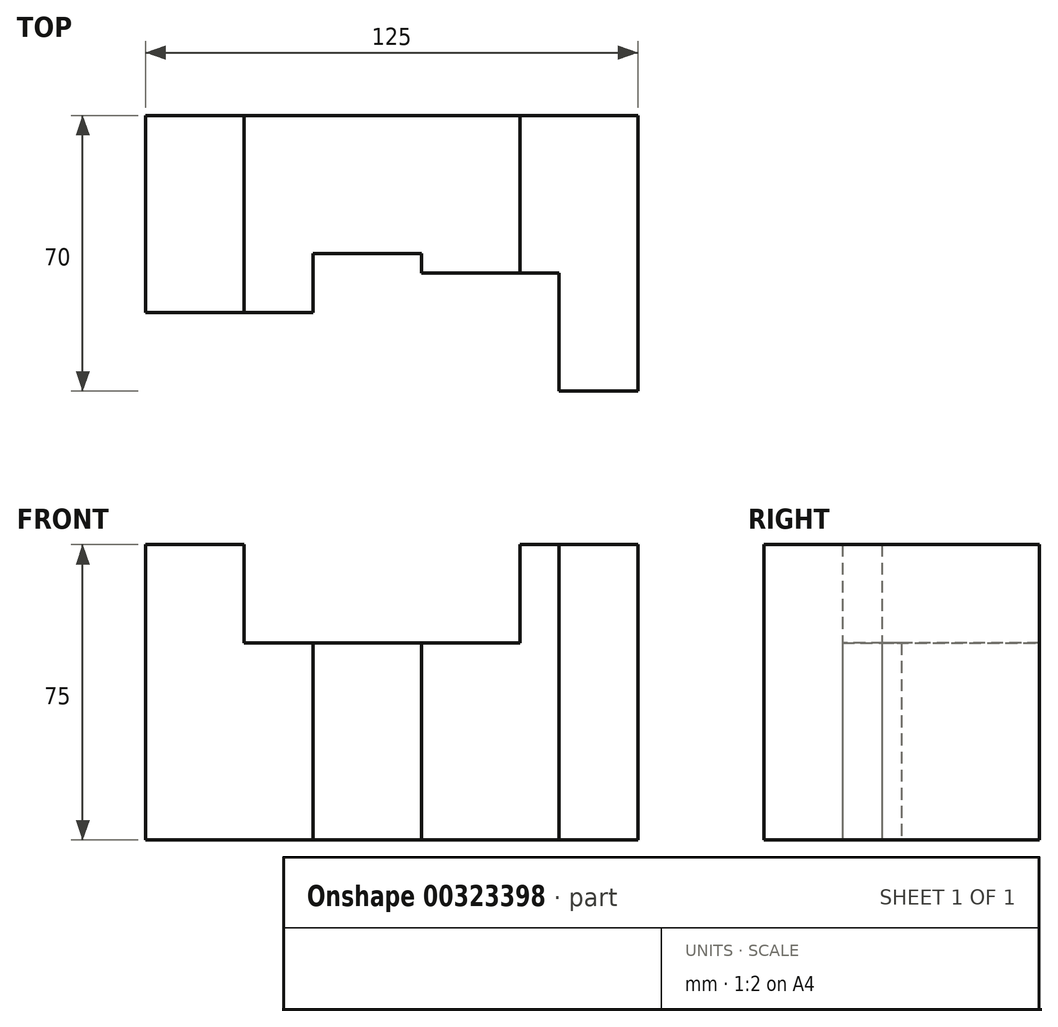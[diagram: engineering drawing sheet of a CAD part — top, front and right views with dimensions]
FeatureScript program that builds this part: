
annotation { "Feature Type Name" : "Feature", "Feature Type Description" : "" }
export const myFeature = defineFeature(function(context is Context, id is Id, definition is map)
    precondition{}
    {
        {
            var Q0;
            Q0=qCreatedBy(makeId("Top.planeOp"),FACE);
            var sketch = newSketch(context, id + "F0", { "sketchPlane" : qUnion([Q0])});
            skLineSegment(sketch, "E0.bottom", {"start": v(0, 0) * mm, "end": v(25, 0) * mm});
            skLineSegment(sketch, "E0.top", {"start": v(0, 50) * mm, "end": v(25, 50) * mm});
            skLineSegment(sketch, "E0.left", {"start": v(0, 0) * mm, "end": v(0, 50) * mm});
            skLineSegment(sketch, "E0.right", {"start": v(25, 0) * mm, "end": v(25, 50) * mm});
            skSolve(sketch);
        }
        {
            var Q0;
            Q0 = qSketchRegion(id + "F0", true);
            extrude(context, id + "F1", {"entities" : qUnion([Q0]), "depth" : (15 * 5) * mm});
        }
        {
            var Q0;
            Q0=qCreatedBy(makeId("Top.planeOp"),FACE);
            var sketch = newSketch(context, id + "F2", { "sketchPlane" : qUnion([Q0])});
            skLineSegment(sketch, "E1", {"start": v(25, 0) * mm, "end": v(25, 50) * mm});
            skLineSegment(sketch, "E2", {"start": v(25, 50) * mm, "end": v(95, 50) * mm});
            skLineSegment(sketch, "E3", {"start": v(95, 50) * mm, "end": v(95, 10) * mm});
            skLineSegment(sketch, "E4", {"start": v(95, 10) * mm, "end": v(70, 10) * mm});
            skLineSegment(sketch, "E5", {"start": v(70, 10) * mm, "end": v(70, 15) * mm});
            skLineSegment(sketch, "E6", {"start": v(70, 15) * mm, "end": v(42.5, 15) * mm});
            skLineSegment(sketch, "E7", {"start": v(42.5, 15) * mm, "end": v(42.5, 0) * mm});
            skLineSegment(sketch, "E8", {"start": v(42.5, 0) * mm, "end": v(25, 0) * mm});
            skSolve(sketch);
        }
        {
            var Q0;
            Q0 = qSketchRegion(id + "F2", true);
            extrude(context, id + "F3", {"entities" : qUnion([Q0]), "operationType" : NewBodyOperationType.ADD, "depth" : 50 * mm});
        }
        {
            var Q0;
            Q0=qCreatedBy(makeId("Top.planeOp"),FACE);
            var sketch = newSketch(context, id + "F4", { "sketchPlane" : qUnion([Q0])});
            skLineSegment(sketch, "E9", {"start": v(95, 10) * mm, "end": v(105, 10) * mm});
            skLineSegment(sketch, "E10", {"start": v(95, 10) * mm, "end": v(95, 50) * mm});
            skLineSegment(sketch, "E11", {"start": v(95, 50) * mm, "end": v(125, 50) * mm});
            skLineSegment(sketch, "E12", {"start": v(125, 50) * mm, "end": v(125, -20) * mm});
            skLineSegment(sketch, "E13", {"start": v(105, 10) * mm, "end": v(105, -20) * mm});
            skLineSegment(sketch, "E14", {"start": v(105, -20) * mm, "end": v(125, -20) * mm});
            skSolve(sketch);
        }
        {
            var Q0;
            Q0 = qSketchRegion(id + "F4", true);
            extrude(context, id + "F5", {"entities" : qUnion([Q0]), "operationType" : NewBodyOperationType.ADD, "depth" : 75 * mm});
        }
    });
